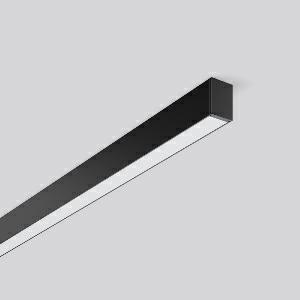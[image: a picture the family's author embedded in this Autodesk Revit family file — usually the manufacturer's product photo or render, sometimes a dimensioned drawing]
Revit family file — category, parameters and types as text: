
# Revit family: less_is_more_27_312196_003_ee4e
name_source: partatom
category: Lighting Fixtures
units: mm (PartAtom-declared; Revit-internal decimal feet)

## family parameters
Cut with Voids When Loaded = No
Host = Face
Light Source = No
Part Type = Normal
Room Calculation Point = No
Round Connector Dimension = Use Diameter
Shared = No

## types (1)
- LESS IS MORE 27 (1 x LED Modul 830, 1600 lm, 3000)
    Apparent Load = 29 VA
    CIE Flux Codes = 48 79 96 100 100
    Color Rendering = 80
    Color Temperature = 3000
    Default Elevation = 1800 mm
    Description = Series: LESS IS MORE 27
Ceiling and wall luminaire with slim design. Housing: extruded aluminium profile, powder-coated. End cap aluminium powder-coated. Diffuser made of non-yellowing plastic (PMMA), opal. Suitable for Ceiling mounting, Wall (surface). External driver with connecting cable. 
Colour: deep black, matt (RAL 9005)
Length: 1012 mm
Width: 28 mm
Height: 38 mm
Lamp: LED
Socket: without socket
Colour temperature: 3000K
Colour rendering index (CRI): 82
System power: 29 W
Rated luminous flux: 1600 lm
Luminous efficiency: 55 lm/W
Control gear: Regulated power supply
Protection class: II
Type of protection: IP 20
    Height = 38 mm
    Lamp = 1 x LED Modul 830
    Lamp Light Flux = 1600 lm
    Lamp count = 1
    Length = 1012 mm
    Lifetime = 50000 h
    Luminous efficacy = 55 lm/W
    Manufacturer = RZB
    ModVariant = No
    Model = 312196.003
    Mounting Place = Ceiling, Wall
    Mounting Type = Surface mounted
    Number of Poles = 1
    OnlyDefault = Yes
    Power Factor = 1
    Product Name = LESS IS MORE 27
    Product group = Surface mounted LED linear luminaires
    ProductGroupID = 307
    Protection Class = Protection class II
    Protection Degree = IP 20
    RLX_Detail_Level = 1
    RLX_Emergency_Light_Flux = 0 lm
    RLX_Emergency_Type = 0
    RLX_Emergency_Type_DB = No
    RlxData = <blob elided: 28609 chars, md5=12f67fd7>
    Socket = socket
    Standby Power = 0 W
    System Light Flux = 1600 lm
    System Power = 29 W
    Type Comments = Product without accessories
    Type Image = 312196.003.jpg
    URL = http://relux.com
    VarID = ---
    Voltage = 230 V
    Voltage Range = 220-240 V
    Weight = 0.00 kg
    Width = 28 mm

## geometry (parser evidence)
native form markers: Blend x4, Sweep x12
no freeform markers — native parametric forms only
